# Revit family: IEK_Зажим соединительный параллельный_Полоса-пруток-полоса_Пруток_Соединение
name_source: partatom
category: Соединительные детали воздуховодов
units: mm (PartAtom-declared; Revit-internal decimal feet)

## family parameters
Всегда вертикально = Да
На основе рабочей плоскости = Нет
Общий = Нет
При загрузке вырезать с полостями = Нет
Размер круглого соединителя = Использовать диаметр
Тип детали = Соединение

## types (1)
- 20-40_8-10_Сталь оцинкованная
    ADSK_URL страницы изделия = https://www.iek.ru
    ADSK_Версия Revit = 2019
    ADSK_Версия семейства = 1.0
    ADSK_Группирование = VIII. ЭЛЕМЕНТЫ ВНЕШНЕЙ МОЛНИЕЗАЩИТЫ
    ADSK_Единица измерения = шт
    ADSK_Завод-изготовитель = IEK
    ADSK_Код изделия = ZCC24-11-1-16-40
    ADSK_Масса = 0.136
    ADSK_Материал = Сталь оцинкованная
    ADSK_Материал наименование = Сталь оцинкованная
    ADSK_Наименование = Зажим соед. параллельный пол./прут.—пол. оц. сталь IEK
    IEK_URL = https://www.iek.ru
    IEK_Описание = Зажим соединительный параллельный полоса/пруток – полоса товарного знака IEK используется для соединения плоских или круглых проводников параллельным способом. Наличие разделительной пластины позволяет предотвратить контактную коррозию в воздухе между металлами.
    IEK_Цена за единицу = 469.2
    KSI_CMa_Строительные материалы = 24.10.35.000.08.3.05.06-0001
